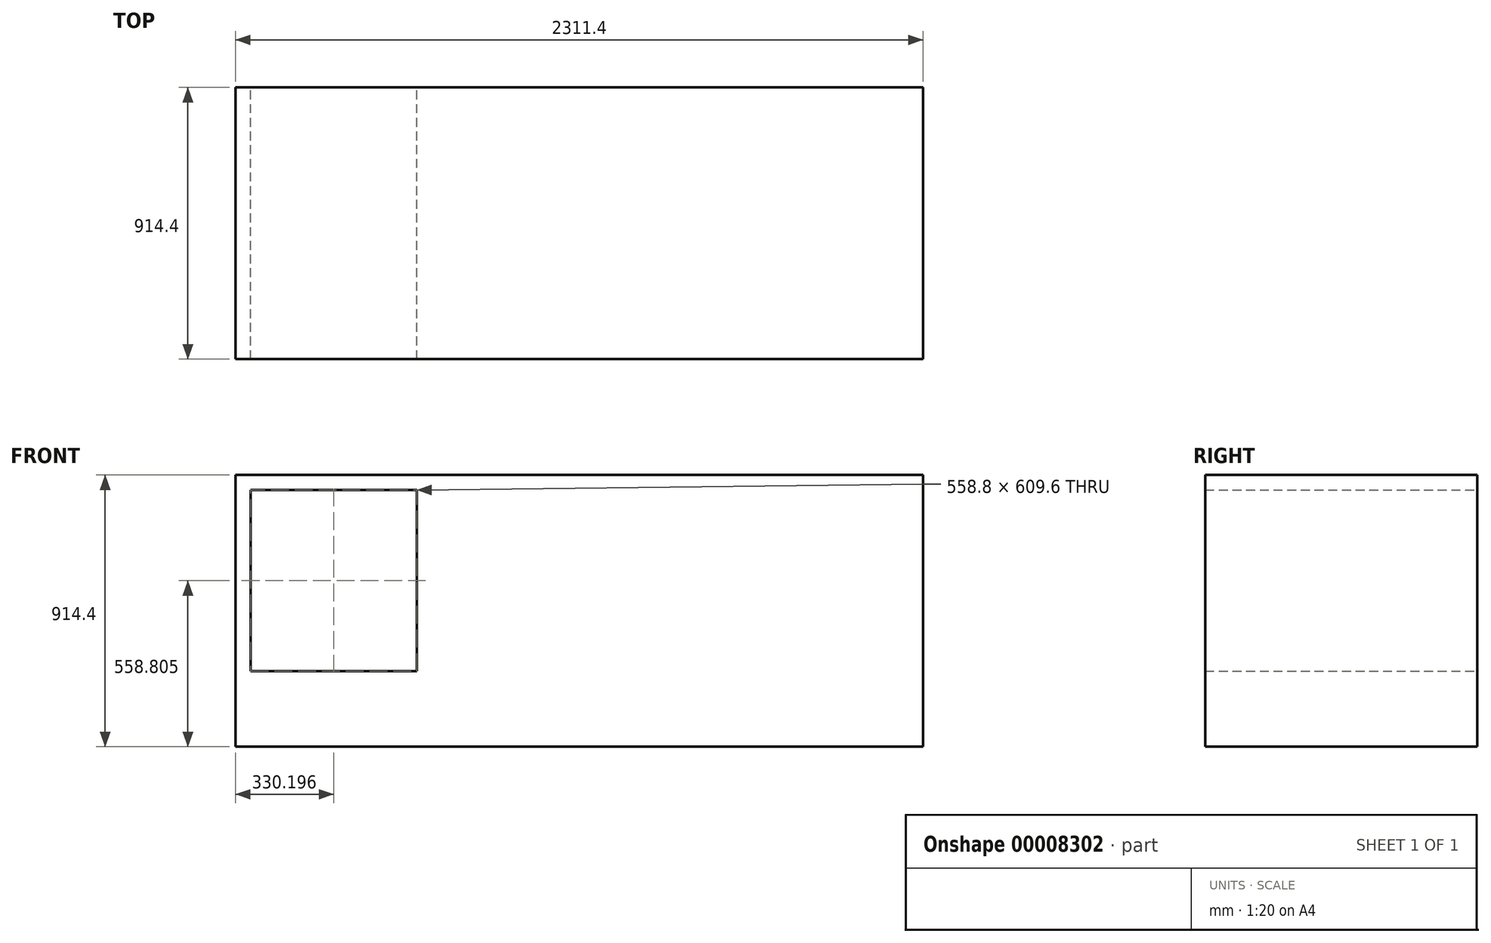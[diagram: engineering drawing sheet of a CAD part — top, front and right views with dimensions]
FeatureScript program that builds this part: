
annotation { "Feature Type Name" : "Feature", "Feature Type Description" : "" }
export const myFeature = defineFeature(function(context is Context, id is Id, definition is map)
    precondition{}
    {
        {
            var Q0;
            Q0=qCreatedBy(makeId("Front.planeOp"),FACE);
            var sketch = newSketch(context, id + "F0", { "sketchPlane" : qUnion([Q0])});
            skLineSegment(sketch, "E0.bottom", {"start": v(-88.14, 853.78) * mm, "end": v(2223.26, 853.78) * mm});
            skLineSegment(sketch, "E0.top", {"start": v(-88.14, -60.62) * mm, "end": v(2223.26, -60.62) * mm});
            skLineSegment(sketch, "E0.left", {"start": v(-88.14, 853.78) * mm, "end": v(-88.14, -60.62) * mm});
            skLineSegment(sketch, "E0.right", {"start": v(2223.26, 853.78) * mm, "end": v(2223.26, -60.62) * mm});
            skLineSegment(sketch, "E1.bottom", {"start": v(-37.34, 802.98) * mm, "end": v(521.46, 802.98) * mm});
            skLineSegment(sketch, "E1.top", {"start": v(-37.34, 193.38) * mm, "end": v(521.46, 193.38) * mm});
            skLineSegment(sketch, "E1.left", {"start": v(-37.34, 802.98) * mm, "end": v(-37.34, 193.38) * mm});
            skLineSegment(sketch, "E1.right", {"start": v(521.46, 802.98) * mm, "end": v(521.46, 193.38) * mm});
            skLineSegment(sketch, "E2", {"start": v(286.85, 802.98) * mm, "end": v(286.85, 853.78) * mm, "construction": true});
            skLineSegment(sketch, "E3", {"start": v(-37.34, 498.18) * mm, "end": v(-88.14, 498.18) * mm});
            skSolve(sketch);
        }
        {
            var Q0;
            {var subQ7=sQuery(id+"F0.wireOp",EDGE,"E0.bottom");Q0=makeQuery(id+"F0.imprint","IMPRINT",FACE,{"disambiguationData":[TD([[makeQuery(id+"F0.imprint","IMPRINT",EDGE,{"derivedFrom":subQ7}),-1.0]])]});}
            extrude(context, id + "F1", {"entities" : qUnion([Q0]), "depth" : 914.4 * mm});
        }
    });
